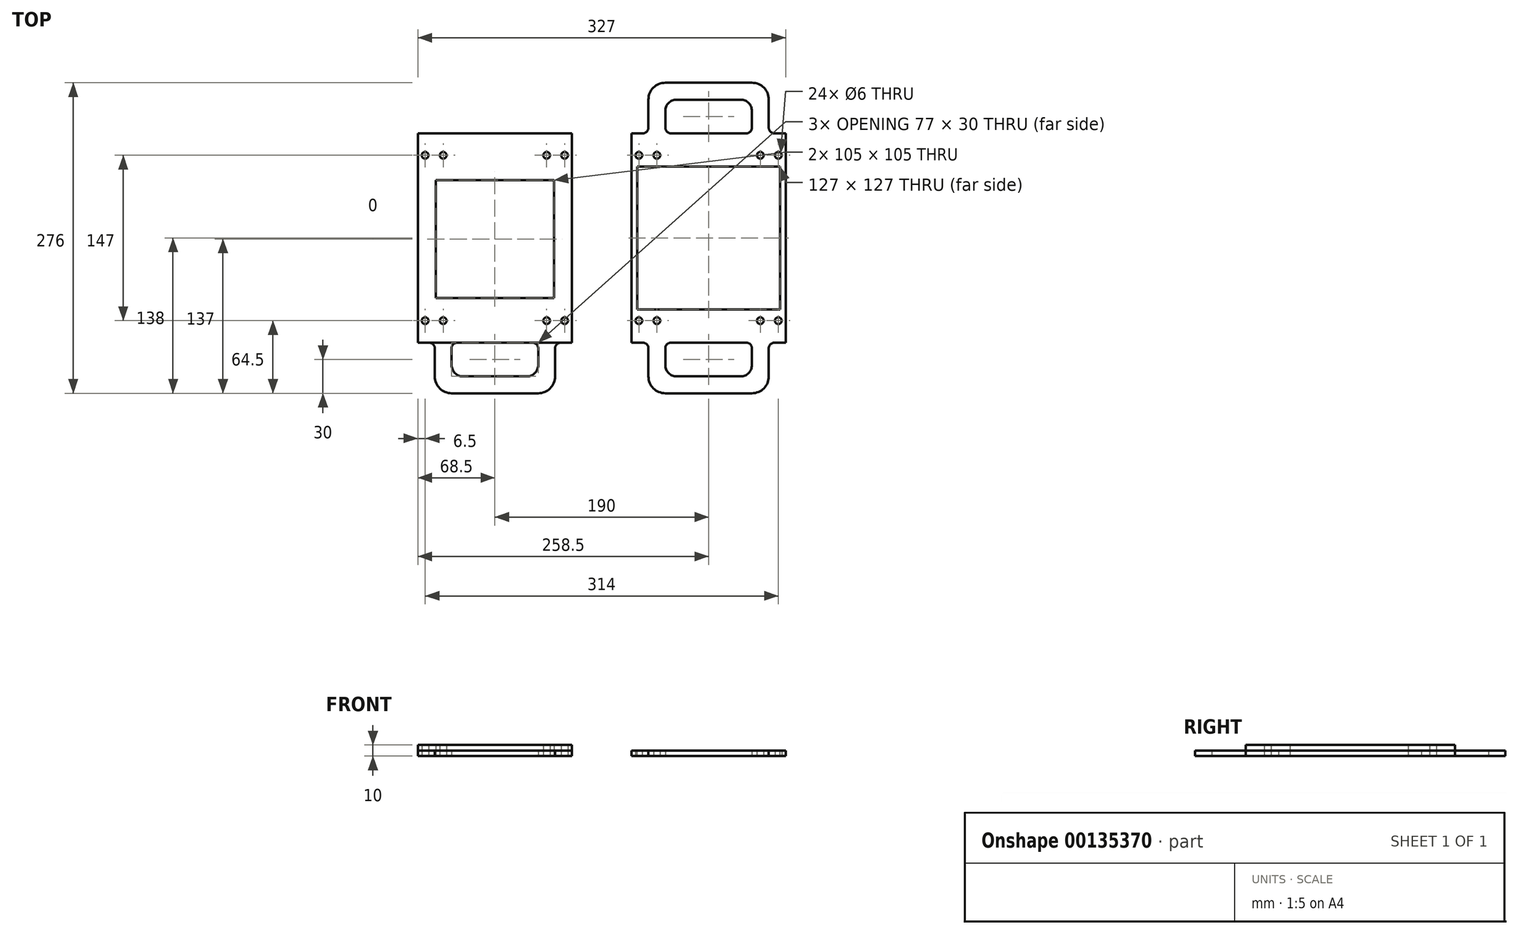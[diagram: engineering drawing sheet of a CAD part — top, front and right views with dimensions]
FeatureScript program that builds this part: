
annotation { "Feature Type Name" : "Feature", "Feature Type Description" : "" }
export const myFeature = defineFeature(function(context is Context, id is Id, definition is map)
    precondition{}
    {
        {
            var Q0;
            Q0=qCreatedBy(makeId("Top.planeOp"),FACE);
            var sketch = newSketch(context, id + "F0", { "sketchPlane" : qUnion([Q0])});
            skLineSegment(sketch, "E0.bottom", {"start": v(0, 0) * mm, "end": v(10, 0) * mm});
            skLineSegment(sketch, "E0.top", {"start": v(0, 186) * mm, "end": v(10, 186) * mm});
            skLineSegment(sketch, "E0.left", {"start": v(0, 0) * mm, "end": v(0, 186) * mm});
            skLineSegment(sketch, "E0.right", {"start": v(137, 0) * mm, "end": v(137, 186) * mm});
            skLineSegment(sketch, "E1.bottom", {"start": v(16, 144.5) * mm, "end": v(121, 144.5) * mm});
            skLineSegment(sketch, "E1.top", {"start": v(16, 39.5) * mm, "end": v(121, 39.5) * mm});
            skLineSegment(sketch, "E1.left", {"start": v(16, 144.5) * mm, "end": v(16, 39.5) * mm});
            skLineSegment(sketch, "E1.right", {"start": v(121, 144.5) * mm, "end": v(121, 39.5) * mm});
            skPoint(sketch, "E2", {"position": v(6.5, 166.5) * mm});
            skPoint(sketch, "E3", {"position": v(22.5, 166.5) * mm});
            skLineSegment(sketch, "E4", {"start": v(6.5, 166.5) * mm, "end": v(22.5, 166.5) * mm, "construction": true});
            skCircle(sketch, "E5", {"center": v(6.5, 166.5) * mm, "radius": 3 * mm});
            skCircle(sketch, "E6", {"center": v(22.5, 166.5) * mm, "radius": 3 * mm});
            skCircle(sketch, "E7.0.1.0", {"center": v(6.5, 19.5) * mm, "radius": 3 * mm});
            skPoint(sketch, "E7.0.1.1", {"position": v(22.5, 19.5) * mm});
            skCircle(sketch, "E7.0.1.2", {"center": v(22.5, 19.5) * mm, "radius": 3 * mm});
            skCircle(sketch, "E7.1.0.0", {"center": v(114.5, 166.5) * mm, "radius": 3 * mm});
            skPoint(sketch, "E7.1.0.1", {"position": v(130.5, 166.5) * mm});
            skCircle(sketch, "E7.1.0.2", {"center": v(130.5, 166.5) * mm, "radius": 3 * mm});
            skCircle(sketch, "E7.1.1.0", {"center": v(114.5, 19.5) * mm, "radius": 3 * mm});
            skPoint(sketch, "E7.1.1.1", {"position": v(130.5, 19.5) * mm});
            skCircle(sketch, "E7.1.1.2", {"center": v(130.5, 19.5) * mm, "radius": 3 * mm});
            skLineSegment(sketch, "E7.direction1", {"start": v(6.5, 166.5) * mm, "end": v(114.5, 166.5) * mm, "construction": true});
            skLineSegment(sketch, "E7.direction2", {"start": v(6.5, 166.5) * mm, "end": v(6.5, 19.5) * mm, "construction": true});
            skLineSegment(sketch, "E8.left", {"start": v(15, -5) * mm, "end": v(15, -30) * mm});
            skLineSegment(sketch, "E8.right", {"start": v(30, -5) * mm, "end": v(30, -20) * mm});
            skLineSegment(sketch, "E9.top", {"start": v(40, -30) * mm, "end": v(97, -30) * mm});
            skLineSegment(sketch, "E10.left", {"start": v(107, -20) * mm, "end": v(107, -5) * mm});
            skLineSegment(sketch, "E10.right", {"start": v(122, -30) * mm, "end": v(122, -5) * mm});
            skLineSegment(sketch, "E11.trimOffspring", {"start": v(35, 0) * mm, "end": v(102, 0) * mm});
            skLineSegment(sketch, "E12.trimOffspring", {"start": v(127, 0) * mm, "end": v(137, 0) * mm});
            skLineSegment(sketch, "E13", {"start": v(30, -45) * mm, "end": v(107, -45) * mm});
            skPoint(sketch, "E14.visualSharp", {"position": v(122, 0) * mm});
            skArc(sketch, "E14.filletArc", {"start": v(127, 0) * mm, "mid": v(123.46, -1.46) * mm, "end": v(122, -5) * mm});
            skPoint(sketch, "E15.visualSharp", {"position": v(15, 0) * mm});
            skArc(sketch, "E15.filletArc", {"start": v(15, -5) * mm, "mid": v(13.54, -1.46) * mm, "end": v(10, 0) * mm});
            skPoint(sketch, "E16.visualSharp", {"position": v(30, -30) * mm});
            skArc(sketch, "E16.filletArc", {"start": v(30, -20) * mm, "mid": v(32.93, -27.07) * mm, "end": v(40, -30) * mm});
            skPoint(sketch, "E17.visualSharp", {"position": v(107, -30) * mm});
            skArc(sketch, "E17.filletArc", {"start": v(97, -30) * mm, "mid": v(104.07, -27.07) * mm, "end": v(107, -20) * mm});
            skPoint(sketch, "E18.visualSharp", {"position": v(15, -45) * mm});
            skArc(sketch, "E18.filletArc", {"start": v(15, -30) * mm, "mid": v(19.4, -40.6) * mm, "end": v(30, -45) * mm});
            skPoint(sketch, "E19.visualSharp", {"position": v(122, -45) * mm});
            skArc(sketch, "E19.filletArc", {"start": v(107, -45) * mm, "mid": v(117.6, -40.6) * mm, "end": v(122, -30) * mm});
            skLineSegment(sketch, "E20", {"start": v(0, 93) * mm, "end": v(137, 93) * mm, "construction": true});
            skArc(sketch, "E21.MirrorCS", {"start": v(15, 191) * mm, "mid": v(13.54, 187.46) * mm, "end": v(10, 186) * mm});
            skLineSegment(sketch, "E22.MirrorCS", {"start": v(15, 191) * mm, "end": v(15, 216) * mm});
            skLineSegment(sketch, "E23.MirrorCS", {"start": v(30, 191) * mm, "end": v(30, 206) * mm});
            skArc(sketch, "E24.MirrorCS", {"start": v(15, 216) * mm, "mid": v(19.4, 226.6) * mm, "end": v(30, 231) * mm});
            skArc(sketch, "E25.MirrorCS", {"start": v(30, 206) * mm, "mid": v(32.93, 213.07) * mm, "end": v(40, 216) * mm});
            skLineSegment(sketch, "E26.MirrorCS", {"start": v(30, 231) * mm, "end": v(107, 231) * mm});
            skLineSegment(sketch, "E27.MirrorCS", {"start": v(40, 216) * mm, "end": v(97, 216) * mm});
            skArc(sketch, "E28.MirrorCS", {"start": v(97, 216) * mm, "mid": v(104.07, 213.07) * mm, "end": v(107, 206) * mm});
            skArc(sketch, "E29.MirrorCS", {"start": v(107, 231) * mm, "mid": v(117.6, 226.6) * mm, "end": v(122, 216) * mm});
            skLineSegment(sketch, "E30.MirrorCS", {"start": v(122, 216) * mm, "end": v(122, 191) * mm});
            skLineSegment(sketch, "E31.MirrorCS", {"start": v(107, 206) * mm, "end": v(107, 191) * mm});
            skArc(sketch, "E32.MirrorCS", {"start": v(127, 186) * mm, "mid": v(123.46, 187.46) * mm, "end": v(122, 191) * mm});
            skLineSegment(sketch, "E33.trimOffspring", {"start": v(35, 186) * mm, "end": v(102, 186) * mm});
            skLineSegment(sketch, "E34.trimOffspring", {"start": v(127, 186) * mm, "end": v(137, 186) * mm});
            skPoint(sketch, "E35.visualSharp", {"position": v(30, 0) * mm});
            skArc(sketch, "E35.filletArc", {"start": v(35, 0) * mm, "mid": v(31.46, -1.46) * mm, "end": v(30, -5) * mm});
            skPoint(sketch, "E36.visualSharp", {"position": v(107, 0) * mm});
            skArc(sketch, "E36.filletArc", {"start": v(107, -5) * mm, "mid": v(105.54, -1.46) * mm, "end": v(102, 0) * mm});
            skArc(sketch, "E37.MirrorCS", {"start": v(35, 186) * mm, "mid": v(31.46, 187.46) * mm, "end": v(30, 191) * mm});
            skArc(sketch, "E38.MirrorCS", {"start": v(107, 191) * mm, "mid": v(105.54, 187.46) * mm, "end": v(102, 186) * mm});
            skPoint(sketch, "E39.orphan", {"position": v(30, 186) * mm});
            skPoint(sketch, "E40.orphan", {"position": v(107, 186) * mm});
            skLineSegment(sketch, "E41", {"start": v(10, 186) * mm, "end": v(35, 186) * mm});
            skLineSegment(sketch, "E42", {"start": v(102, 186) * mm, "end": v(127, 186) * mm});
            skLineSegment(sketch, "E43", {"start": v(10, 0) * mm, "end": v(35, 0) * mm});
            skLineSegment(sketch, "E44", {"start": v(102, 0) * mm, "end": v(127, 0) * mm});
            skSolve(sketch);
        }
        {
            var Q0;
            Q0=makeQuery(id+"F0.imprint","IMPRINT",FACE,{"disambiguationData":[TD([[makeQuery(id+"F0.imprint","IMPRINT",EDGE,{"derivedFrom":sQuery(id+"F0.wireOp",EDGE,"E0.top")}),-1.0]])]});
            var Q1;
            Q1=makeQuery(id+"F0.imprint","IMPRINT",FACE,{"disambiguationData":[TD([[makeQuery(id+"F0.imprint","IMPRINT",EDGE,{"derivedFrom":sQuery(id+"F0.wireOp",EDGE,"E21.MirrorCS")}),1.0]])]});
            var Q2;
            Q2=makeQuery(id+"F0.imprint","IMPRINT",FACE,{"disambiguationData":[TD([[makeQuery(id+"F0.imprint","IMPRINT",EDGE,{"derivedFrom":sQuery(id+"F0.wireOp",EDGE,"E8.left")}),1.0]])]});
            extrude(context, id + "F1", {"entities" : qUnion([Q0, Q1, Q2]), "depth" : 5 * mm});
        }
        {
            var Q0;
            Q0=qCreatedBy(makeId("Top.planeOp"),FACE);
            var sketch = newSketch(context, id + "F2", { "sketchPlane" : qUnion([Q0])});
            skLineSegment(sketch, "E45.left", {"start": v(190, 0) * mm, "end": v(190, 186) * mm});
            skLineSegment(sketch, "E45.right", {"start": v(327, 0) * mm, "end": v(327, 186) * mm});
            skLineSegment(sketch, "E46", {"start": v(196.5, 166.5) * mm, "end": v(212.5, 166.5) * mm, "construction": true});
            skCircle(sketch, "E47", {"center": v(196.5, 166.5) * mm, "radius": 3 * mm});
            skCircle(sketch, "E48", {"center": v(212.5, 166.5) * mm, "radius": 3 * mm});
            skCircle(sketch, "E49.0.1.0", {"center": v(196.5, 19.5) * mm, "radius": 3 * mm});
            skCircle(sketch, "E49.0.1.1", {"center": v(212.5, 19.5) * mm, "radius": 3 * mm});
            skCircle(sketch, "E49.1.0.0", {"center": v(304.5, 166.5) * mm, "radius": 3 * mm});
            skCircle(sketch, "E49.1.0.1", {"center": v(320.5, 166.5) * mm, "radius": 3 * mm});
            skCircle(sketch, "E49.1.1.0", {"center": v(304.5, 19.5) * mm, "radius": 3 * mm});
            skCircle(sketch, "E49.1.1.1", {"center": v(320.5, 19.5) * mm, "radius": 3 * mm});
            skLineSegment(sketch, "E49.direction1", {"start": v(196.5, 166.5) * mm, "end": v(304.5, 166.5) * mm, "construction": true});
            skLineSegment(sketch, "E49.direction2", {"start": v(196.5, 166.5) * mm, "end": v(196.5, 19.5) * mm, "construction": true});
            skLineSegment(sketch, "E50", {"start": v(190, 93) * mm, "end": v(327, 93) * mm, "construction": true});
            skLineSegment(sketch, "E51", {"start": v(190, 0) * mm, "end": v(200, 0) * mm});
            skLineSegment(sketch, "E52", {"start": v(220, -5) * mm, "end": v(220, -20) * mm});
            skLineSegment(sketch, "E53", {"start": v(230, -30) * mm, "end": v(287, -30) * mm});
            skLineSegment(sketch, "E54", {"start": v(297, -20) * mm, "end": v(297, -5) * mm});
            skLineSegment(sketch, "E55", {"start": v(205, -5) * mm, "end": v(205, -30) * mm});
            skLineSegment(sketch, "E56", {"start": v(220, -45) * mm, "end": v(297, -45) * mm});
            skLineSegment(sketch, "E57", {"start": v(312, -30) * mm, "end": v(312, -5) * mm});
            skLineSegment(sketch, "E58.trimOffspring", {"start": v(225, 0) * mm, "end": v(292, 0) * mm});
            skLineSegment(sketch, "E59.trimOffspring", {"start": v(317, 0) * mm, "end": v(327, 0) * mm});
            skPoint(sketch, "E60.visualSharp", {"position": v(205, -45) * mm});
            skArc(sketch, "E60.filletArc", {"start": v(205, -30) * mm, "mid": v(209.4, -40.6) * mm, "end": v(220, -45) * mm});
            skArc(sketch, "E61.filletArc", {"start": v(220, -20) * mm, "mid": v(222.93, -27.07) * mm, "end": v(230, -30) * mm});
            skPoint(sketch, "E62.visualSharp", {"position": v(312, -45) * mm});
            skArc(sketch, "E62.filletArc", {"start": v(297, -45) * mm, "mid": v(307.6, -40.6) * mm, "end": v(312, -30) * mm});
            skArc(sketch, "E63.filletArc", {"start": v(287, -30) * mm, "mid": v(294.07, -27.07) * mm, "end": v(297, -20) * mm});
            skPoint(sketch, "E64.visualSharp", {"position": v(205, 0) * mm});
            skArc(sketch, "E64.filletArc", {"start": v(205, -5) * mm, "mid": v(203.54, -1.46) * mm, "end": v(200, 0) * mm});
            skPoint(sketch, "E65.visualSharp", {"position": v(220, 0) * mm});
            skArc(sketch, "E65.filletArc", {"start": v(225, 0) * mm, "mid": v(221.46, -1.46) * mm, "end": v(220, -5) * mm});
            skPoint(sketch, "E66.visualSharp", {"position": v(297, 0) * mm});
            skArc(sketch, "E66.filletArc", {"start": v(297, -5) * mm, "mid": v(295.54, -1.46) * mm, "end": v(292, 0) * mm});
            skPoint(sketch, "E67.visualSharp", {"position": v(312, 0) * mm});
            skArc(sketch, "E67.filletArc", {"start": v(317, 0) * mm, "mid": v(313.46, -1.46) * mm, "end": v(312, -5) * mm});
            skLineSegment(sketch, "E68.MirrorCS", {"start": v(220, 191) * mm, "end": v(220, 206) * mm});
            skArc(sketch, "E69.MirrorCS", {"start": v(317, 186) * mm, "mid": v(313.46, 187.46) * mm, "end": v(312, 191) * mm});
            skLineSegment(sketch, "E70.MirrorCS", {"start": v(297, 206) * mm, "end": v(297, 191) * mm});
            skArc(sketch, "E71.MirrorCS", {"start": v(205, 191) * mm, "mid": v(203.54, 187.46) * mm, "end": v(200, 186) * mm});
            skArc(sketch, "E72.MirrorCS", {"start": v(297, 191) * mm, "mid": v(295.54, 187.46) * mm, "end": v(292, 186) * mm});
            skArc(sketch, "E73.MirrorCS", {"start": v(225, 186) * mm, "mid": v(221.46, 187.46) * mm, "end": v(220, 191) * mm});
            skPoint(sketch, "E74.MirrorP", {"position": v(205, 231) * mm});
            skLineSegment(sketch, "E75.MirrorCS", {"start": v(230, 216) * mm, "end": v(287, 216) * mm});
            skPoint(sketch, "E76.MirrorP", {"position": v(297, 186) * mm});
            skPoint(sketch, "E77.MirrorP", {"position": v(297, 216) * mm});
            skLineSegment(sketch, "E78.MirrorCS", {"start": v(312, 216) * mm, "end": v(312, 191) * mm});
            skPoint(sketch, "E79.MirrorP", {"position": v(312, 186) * mm});
            skLineSegment(sketch, "E80.MirrorCS", {"start": v(220, 231) * mm, "end": v(297, 231) * mm});
            skPoint(sketch, "E81.MirrorP", {"position": v(205, 186) * mm});
            skPoint(sketch, "E82.MirrorP", {"position": v(220, 186) * mm});
            skLineSegment(sketch, "E83.MirrorCS", {"start": v(225, 186) * mm, "end": v(292, 186) * mm});
            skPoint(sketch, "E84.MirrorP", {"position": v(220, 216) * mm});
            skArc(sketch, "E85.MirrorCS", {"start": v(220, 206) * mm, "mid": v(222.93, 213.07) * mm, "end": v(230, 216) * mm});
            skArc(sketch, "E86.MirrorCS", {"start": v(297, 231) * mm, "mid": v(307.6, 226.6) * mm, "end": v(312, 216) * mm});
            skArc(sketch, "E87.MirrorCS", {"start": v(287, 216) * mm, "mid": v(294.07, 213.07) * mm, "end": v(297, 206) * mm});
            skLineSegment(sketch, "E88.MirrorCS", {"start": v(205, 191) * mm, "end": v(205, 216) * mm});
            skArc(sketch, "E89.MirrorCS", {"start": v(205, 216) * mm, "mid": v(209.4, 226.6) * mm, "end": v(220, 231) * mm});
            skPoint(sketch, "E90.MirrorP", {"position": v(312, 231) * mm});
            skLineSegment(sketch, "E91", {"start": v(190, 186) * mm, "end": v(200, 186) * mm});
            skLineSegment(sketch, "E92", {"start": v(317, 186) * mm, "end": v(327, 186) * mm});
            skLineSegment(sketch, "E93", {"start": v(200, 186) * mm, "end": v(225, 186) * mm});
            skLineSegment(sketch, "E94", {"start": v(292, 186) * mm, "end": v(317, 186) * mm});
            skLineSegment(sketch, "E95", {"start": v(200, 0) * mm, "end": v(225, 0) * mm});
            skLineSegment(sketch, "E96", {"start": v(292, 0) * mm, "end": v(317, 0) * mm});
            skSolve(sketch);
        }
        {
            var Q0;
            Q0=makeQuery(id+"F2.imprint","IMPRINT",FACE,{"disambiguationData":[TD([[makeQuery(id+"F2.imprint","IMPRINT",EDGE,{"derivedFrom":sQuery(id+"F2.wireOp",EDGE,"E45.left")}),-1.0]])]});
            var Q1;
            Q1=makeQuery(id+"F2.imprint","IMPRINT",FACE,{"disambiguationData":[TD([[makeQuery(id+"F2.imprint","IMPRINT",EDGE,{"derivedFrom":sQuery(id+"F2.wireOp",EDGE,"E68.MirrorCS")}),1.0]])]});
            var Q2;
            Q2=makeQuery(id+"F2.imprint","IMPRINT",FACE,{"disambiguationData":[TD([[makeQuery(id+"F2.imprint","IMPRINT",EDGE,{"derivedFrom":sQuery(id+"F2.wireOp",EDGE,"E52")}),-1.0]])]});
            extrude(context, id + "F3", {"entities" : qUnion([Q0, Q1, Q2]), "depth" : 5 * mm});
        }
        {
            var Q0;
            Q0=makeQuery(id+"F3.opExtrude","CAP_FACE",FACE,{"disambiguationData":[OSD([sQuery(id+"F2.wireOp",EDGE,"E45.bottom"),sQuery(id+"F2.wireOp",EDGE,"E45.top"),sQuery(id+"F2.wireOp",EDGE,"E45.left"),sQuery(id+"F2.wireOp",EDGE,"E45.right"),sQuery(id+"F2.wireOp",EDGE,"V1kq5ezt-bu6P-pq4Q-Ebpx-DnbHarAls7aT.top"),sQuery(id+"F2.wireOp",EDGE,"V1kq5ezt-bu6P-pq4Q-Ebpx-DnbHarAls7aT.left"),sQuery(id+"F2.wireOp",EDGE,"V1kq5ezt-bu6P-pq4Q-Ebpx-DnbHarAls7aT.right"),sQuery(id+"F2.wireOp",EDGE,"c80427bf-46ff-4ff9-a88c-c6194353407b.trimOffspring"),sQuery(id+"F2.wireOp",EDGE,"dePXb8LH-FlOM-UH92-7kuR-uvjq0zKmV9C9.bottom"),sQuery(id+"F2.wireOp",EDGE,"dePXb8LH-FlOM-UH92-7kuR-uvjq0zKmV9C9.top"),sQuery(id+"F2.wireOp",EDGE,"dePXb8LH-FlOM-UH92-7kuR-uvjq0zKmV9C9.left"),sQuery(id+"F2.wireOp",EDGE,"dePXb8LH-FlOM-UH92-7kuR-uvjq0zKmV9C9.right"),sQuery(id+"F2.wireOp",EDGE,"E47"),sQuery(id+"F2.wireOp",EDGE,"E49.0.1.0"),sQuery(id+"F2.wireOp",EDGE,"E49.1.0.1"),sQuery(id+"F2.wireOp",EDGE,"E49.1.1.1"),sQuery(id+"F2.wireOp",EDGE,"l95b4v01-oRhH-09xq-MRFA-VYvgqwqiPv6y.bottom"),sQuery(id+"F2.wireOp",EDGE,"l95b4v01-oRhH-09xq-MRFA-VYvgqwqiPv6y.left"),sQuery(id+"F2.wireOp",EDGE,"l95b4v01-oRhH-09xq-MRFA-VYvgqwqiPv6y.right"),sQuery(id+"F2.wireOp",EDGE,"251fb07f-8bf7-4ef4-be91-8580ed0a364e.trimOffspring"),sQuery(id+"F2.wireOp",EDGE,"8056b77b-4f80-41d6-8e88-b6e9b90829560.MirrorCS"),sQuery(id+"F2.wireOp",EDGE,"579f555a-73a4-4620-8b59-0c1a563985cb0.MirrorCS"),sQuery(id+"F2.wireOp",EDGE,"8045b23e-1a49-4ee4-8196-db108ad73c2b0.MirrorCS"),sQuery(id+"F2.wireOp",EDGE,"ab39ded7-a6cd-4521-88df-fec0853f96a30.MirrorCS"),sQuery(id+"F2.wireOp",EDGE,"937db496-c466-455c-9d32-e8f3e94e8cfe0.MirrorCS"),sQuery(id+"F2.wireOp",EDGE,"e5d1d98c-ca5a-46aa-b693-3ff14487759a0.MirrorCS")])],"isStart":false});
            var sketch = newSketch(context, id + "F4", { "sketchPlane" : qUnion([Q0])});
            skLineSegment(sketch, "E97.bottom", {"start": v(195, 156.5) * mm, "end": v(322, 156.5) * mm});
            skLineSegment(sketch, "E97.top", {"start": v(195, 29.5) * mm, "end": v(322, 29.5) * mm});
            skLineSegment(sketch, "E97.left", {"start": v(195, 156.5) * mm, "end": v(195, 29.5) * mm});
            skLineSegment(sketch, "E97.right", {"start": v(322, 156.5) * mm, "end": v(322, 29.5) * mm});
            skSolve(sketch);
        }
        {
            var Q0;
            Q0 = qSketchRegion(id + "F4", true);
            extrude(context, id + "F5", {"entities" : qUnion([Q0]), "operationType" : NewBodyOperationType.REMOVE, "oppositeDirection" : true, "depth" : 5 * mm});
        }
        {
            var Q0;
            Q0=makeQuery(id+"F1.opExtrude","CAP_FACE",FACE,{"disambiguationData":[OSD([sQuery(id+"F0.wireOp",EDGE,"E0.bottom"),sQuery(id+"F0.wireOp",EDGE,"E0.top"),sQuery(id+"F0.wireOp",EDGE,"E0.left"),sQuery(id+"F0.wireOp",EDGE,"E0.right"),sQuery(id+"F0.wireOp",EDGE,"E1.bottom"),sQuery(id+"F0.wireOp",EDGE,"E1.top"),sQuery(id+"F0.wireOp",EDGE,"E1.left"),sQuery(id+"F0.wireOp",EDGE,"E1.right"),sQuery(id+"F0.wireOp",EDGE,"E5"),sQuery(id+"F0.wireOp",EDGE,"E6"),sQuery(id+"F0.wireOp",EDGE,"E7.0.1.0"),sQuery(id+"F0.wireOp",EDGE,"E7.0.1.2"),sQuery(id+"F0.wireOp",EDGE,"E7.1.0.0"),sQuery(id+"F0.wireOp",EDGE,"E7.1.0.2"),sQuery(id+"F0.wireOp",EDGE,"E7.1.1.0"),sQuery(id+"F0.wireOp",EDGE,"E7.1.1.2"),sQuery(id+"F0.wireOp",EDGE,"E8.left"),sQuery(id+"F0.wireOp",EDGE,"E8.right"),sQuery(id+"F0.wireOp",EDGE,"E9.top"),sQuery(id+"F0.wireOp",EDGE,"E10.left"),sQuery(id+"F0.wireOp",EDGE,"E10.right"),sQuery(id+"F0.wireOp",EDGE,"E11.trimOffspring"),sQuery(id+"F0.wireOp",EDGE,"E12.trimOffspring"),sQuery(id+"F0.wireOp",EDGE,"E13"),sQuery(id+"F0.wireOp",EDGE,"E14.filletArc"),sQuery(id+"F0.wireOp",EDGE,"E15.filletArc"),sQuery(id+"F0.wireOp",EDGE,"E16.filletArc"),sQuery(id+"F0.wireOp",EDGE,"E17.filletArc"),sQuery(id+"F0.wireOp",EDGE,"E18.filletArc"),sQuery(id+"F0.wireOp",EDGE,"E19.filletArc"),sQuery(id+"F0.wireOp",EDGE,"E21.MirrorCS"),sQuery(id+"F0.wireOp",EDGE,"E22.MirrorCS"),sQuery(id+"F0.wireOp",EDGE,"E23.MirrorCS"),sQuery(id+"F0.wireOp",EDGE,"E24.MirrorCS"),sQuery(id+"F0.wireOp",EDGE,"E25.MirrorCS"),sQuery(id+"F0.wireOp",EDGE,"E26.MirrorCS"),sQuery(id+"F0.wireOp",EDGE,"E27.MirrorCS"),sQuery(id+"F0.wireOp",EDGE,"E28.MirrorCS"),sQuery(id+"F0.wireOp",EDGE,"E29.MirrorCS"),sQuery(id+"F0.wireOp",EDGE,"E30.MirrorCS"),sQuery(id+"F0.wireOp",EDGE,"E31.MirrorCS"),sQuery(id+"F0.wireOp",EDGE,"E32.MirrorCS"),sQuery(id+"F0.wireOp",EDGE,"E33.trimOffspring"),sQuery(id+"F0.wireOp",EDGE,"E34.trimOffspring"),sQuery(id+"F0.wireOp",EDGE,"E35.filletArc"),sQuery(id+"F0.wireOp",EDGE,"E36.filletArc"),sQuery(id+"F0.wireOp",EDGE,"E37.MirrorCS"),sQuery(id+"F0.wireOp",EDGE,"E38.MirrorCS")])],"isStart":false});
            var sketch = newSketch(context, id + "F6", { "sketchPlane" : qUnion([Q0])});
            skLineSegment(sketch, "E98.bottom", {"start": v(0, 186) * mm, "end": v(137, 186) * mm});
            skLineSegment(sketch, "E98.top", {"start": v(0, 0) * mm, "end": v(137, 0) * mm});
            skLineSegment(sketch, "E98.left", {"start": v(0, 186) * mm, "end": v(0, 0) * mm});
            skLineSegment(sketch, "E98.right", {"start": v(137, 186) * mm, "end": v(137, 0) * mm});
            skCircle(sketch, "E99", {"center": v(6.5, 166.5) * mm, "radius": 3 * mm});
            skCircle(sketch, "E100", {"center": v(22.5, 166.5) * mm, "radius": 3 * mm});
            skLineSegment(sketch, "E101.bottom", {"start": v(16, 144.5) * mm, "end": v(121, 144.5) * mm});
            skLineSegment(sketch, "E101.top", {"start": v(16, 39.5) * mm, "end": v(121, 39.5) * mm});
            skLineSegment(sketch, "E101.left", {"start": v(16, 144.5) * mm, "end": v(16, 39.5) * mm});
            skLineSegment(sketch, "E101.right", {"start": v(121, 144.5) * mm, "end": v(121, 39.5) * mm});
            skCircle(sketch, "E102.0.1.0", {"center": v(6.5, 19.5) * mm, "radius": 3 * mm});
            skCircle(sketch, "E102.0.1.1", {"center": v(22.5, 19.5) * mm, "radius": 3 * mm});
            skCircle(sketch, "E102.1.0.0", {"center": v(114.5, 166.5) * mm, "radius": 3 * mm});
            skCircle(sketch, "E102.1.0.1", {"center": v(130.5, 166.5) * mm, "radius": 3 * mm});
            skCircle(sketch, "E102.1.1.0", {"center": v(114.5, 19.5) * mm, "radius": 3 * mm});
            skCircle(sketch, "E102.1.1.1", {"center": v(130.5, 19.5) * mm, "radius": 3 * mm});
            skLineSegment(sketch, "E102.direction1", {"start": v(6.5, 166.5) * mm, "end": v(114.5, 166.5) * mm, "construction": true});
            skLineSegment(sketch, "E102.direction2", {"start": v(6.5, 166.5) * mm, "end": v(6.5, 19.5) * mm, "construction": true});
            skSolve(sketch);
        }
        {
            var Q0;
            {var subQ5=sQuery(id+"F6.wireOp",EDGE,"E98.left");Q0=makeQuery(id+"F6.imprint","IMPRINT",FACE,{"disambiguationData":[TD([[makeQuery(id+"F6.imprint","IMPRINT",EDGE,{"derivedFrom":subQ5}),-1.0]])]});}
            extrude(context, id + "F7", {"entities" : qUnion([Q0]), "depth" : 5 * mm});
        }
    });
